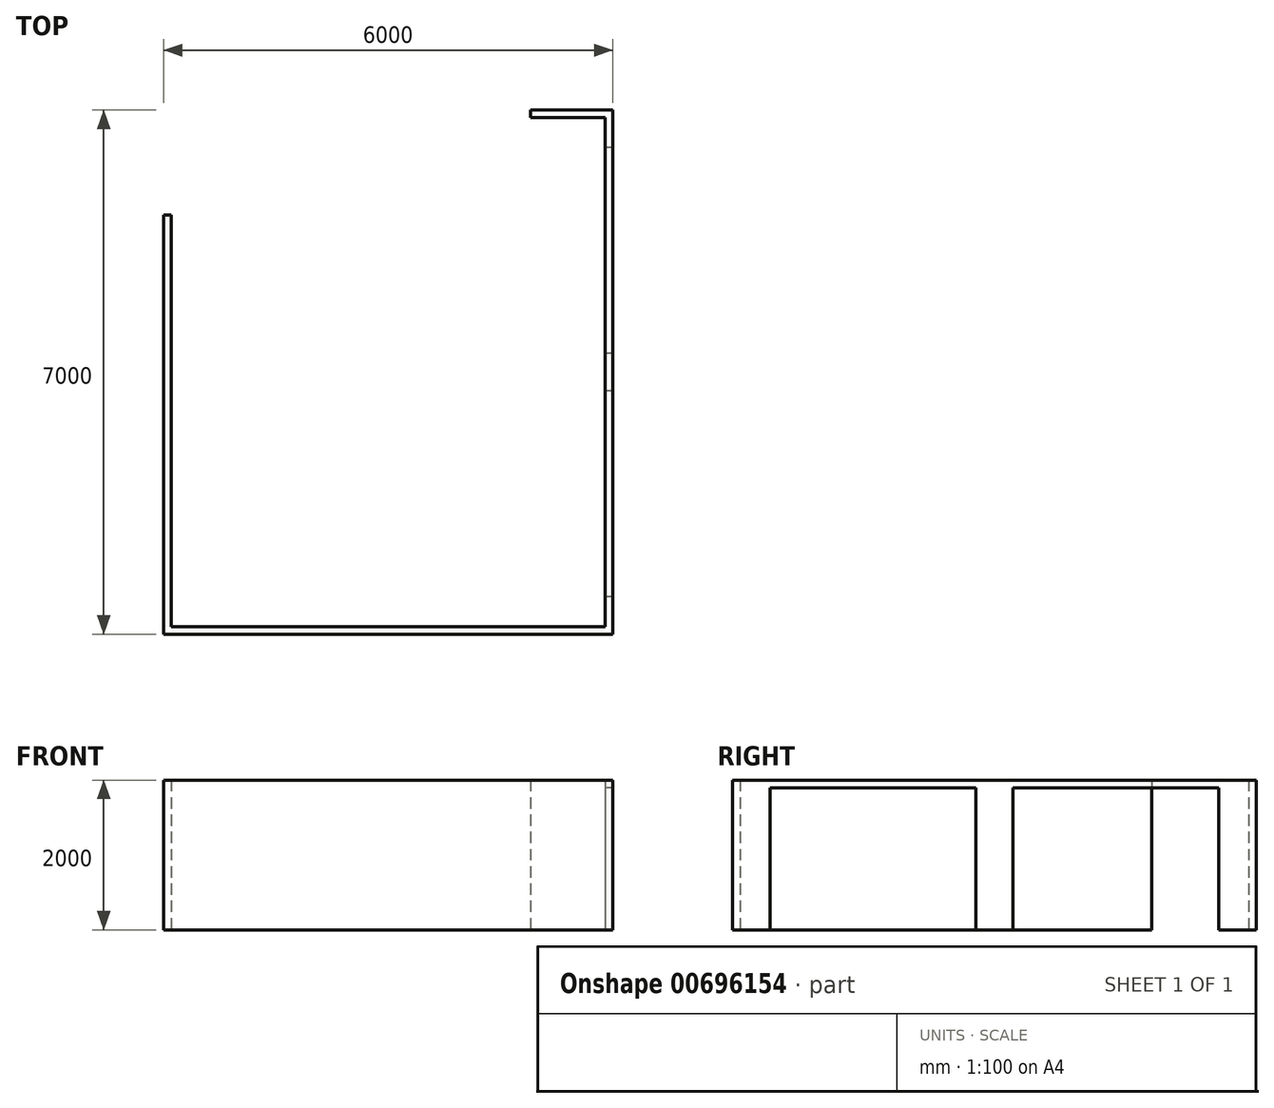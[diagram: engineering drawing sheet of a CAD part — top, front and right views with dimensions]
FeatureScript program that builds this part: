
annotation { "Feature Type Name" : "Feature", "Feature Type Description" : "" }
export const myFeature = defineFeature(function(context is Context, id is Id, definition is map)
    precondition{}
    {
        {
            var Q0;
            Q0=qCreatedBy(makeId("Top.planeOp"),FACE);
            var sketch = newSketch(context, id + "F0", { "sketchPlane" : qUnion([Q0])});
            skLineSegment(sketch, "E0.bottom", {"start": v(1350.15, 3608.57) * mm, "end": v(2450.15, 3608.57) * mm});
            skLineSegment(sketch, "E0.top", {"start": v(-3549.85, -3391.43) * mm, "end": v(2450.15, -3391.43) * mm});
            skLineSegment(sketch, "E0.left", {"start": v(-3549.85, 2208.57) * mm, "end": v(-3549.85, -3391.43) * mm});
            skLineSegment(sketch, "E1", {"start": v(1350.15, 3608.57) * mm, "end": v(1350.15, 3508.57) * mm});
            skLineSegment(sketch, "E2", {"start": v(1350.15, 3508.57) * mm, "end": v(2350.15, 3508.57) * mm});
            skLineSegment(sketch, "E3", {"start": v(-3549.85, 2208.57) * mm, "end": v(-3449.85, 2208.57) * mm});
            skLineSegment(sketch, "E4", {"start": v(-3449.85, 2208.57) * mm, "end": v(-3449.85, -3291.43) * mm});
            skLineSegment(sketch, "E5", {"start": v(-3449.85, -3291.43) * mm, "end": v(2350.15, -3291.43) * mm});
            skPoint(sketch, "E6.end.orphan", {"position": v(2350.15, 408.57) * mm});
            skPoint(sketch, "E7.start.orphan", {"position": v(2350.15, -191.43) * mm});
            skPoint(sketch, "E8.start.orphan", {"position": v(2350.15, -2891.43) * mm});
            skLineSegment(sketch, "E9", {"start": v(2450.15, -3391.43) * mm, "end": v(2450.15, 3608.57) * mm});
            skLineSegment(sketch, "E10", {"start": v(2350.15, 3508.57) * mm, "end": v(2350.15, -3291.43) * mm});
            skSolve(sketch);
        }
        {
            var Q0;
            Q0 = qSketchRegion(id + "F0", true);
            extrude(context, id + "F1", {"entities" : qUnion([Q0]), "depth" : 2000 * mm, "offsetDistance" : 25 * mm});
        }
        {
            var Q0;
            Q0=makeQuery(id+"F1.opExtrude","CAP_FACE",FACE,{"disambiguationData":[OSD([sQuery(id+"F0.wireOp",EDGE,"E0.bottom"),sQuery(id+"F0.wireOp",EDGE,"E0.top"),sQuery(id+"F0.wireOp",EDGE,"E0.left"),sQuery(id+"F0.wireOp",EDGE,"E1"),sQuery(id+"F0.wireOp",EDGE,"E2"),sQuery(id+"F0.wireOp",EDGE,"E3"),sQuery(id+"F0.wireOp",EDGE,"E4"),sQuery(id+"F0.wireOp",EDGE,"E5"),sQuery(id+"F0.wireOp",EDGE,"E9"),sQuery(id+"F0.wireOp",EDGE,"E10")])],"isStart":true});
            var sketch = newSketch(context, id + "F2", { "sketchPlane" : qUnion([Q0])});
            skLineSegment(sketch, "E11.bottom", {"start": v(2450.15, -358.57) * mm, "end": v(2350.15, -358.57) * mm});
            skLineSegment(sketch, "E11.top", {"start": v(2450.15, -3108.57) * mm, "end": v(2350.15, -3108.57) * mm});
            skLineSegment(sketch, "E11.left", {"start": v(2450.15, -358.57) * mm, "end": v(2450.15, -3108.57) * mm});
            skLineSegment(sketch, "E11.right", {"start": v(2350.15, -358.57) * mm, "end": v(2350.15, -3108.57) * mm});
            skLineSegment(sketch, "E12.bottom", {"start": v(2450.15, 2891.43) * mm, "end": v(2350.15, 2891.43) * mm});
            skLineSegment(sketch, "E12.top", {"start": v(2450.15, 141.43) * mm, "end": v(2350.15, 141.43) * mm});
            skLineSegment(sketch, "E12.left", {"start": v(2450.15, 2891.43) * mm, "end": v(2450.15, 141.43) * mm});
            skLineSegment(sketch, "E12.right", {"start": v(2350.15, 2891.43) * mm, "end": v(2350.15, 141.43) * mm});
            skSolve(sketch);
        }
        {
            var Q0;
            Q0 = qSketchRegion(id + "F2", true);
            extrude(context, id + "F3", {"entities" : qUnion([Q0]), "operationType" : NewBodyOperationType.REMOVE, "oppositeDirection" : true, "depth" : 1900 * mm, "offsetDistance" : 25 * mm});
        }
    });
